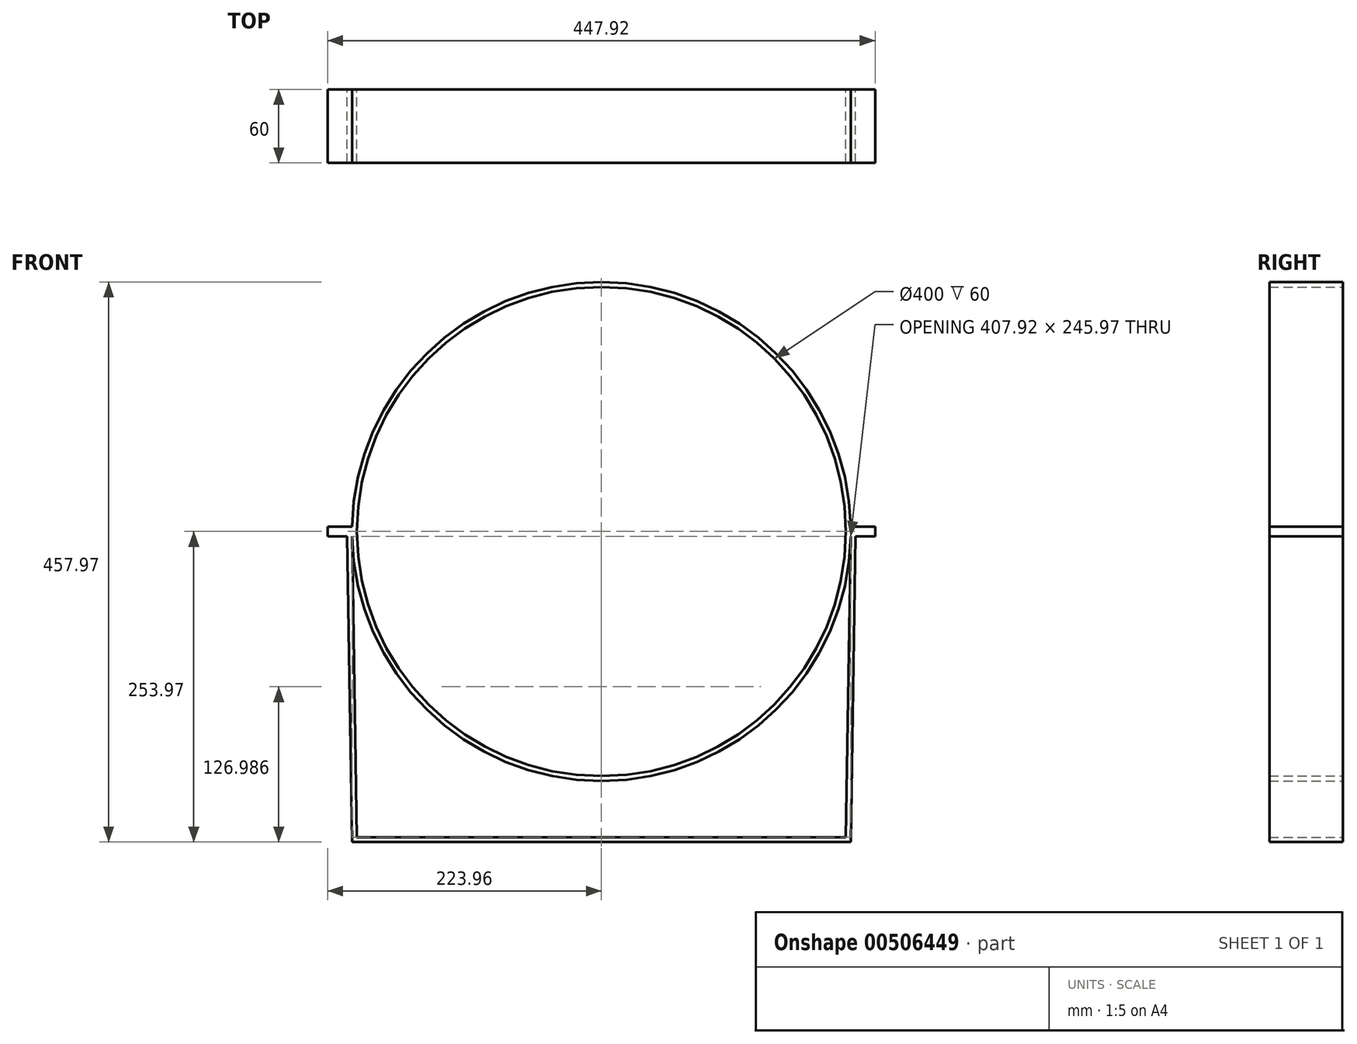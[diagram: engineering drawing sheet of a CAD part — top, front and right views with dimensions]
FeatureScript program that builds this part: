
annotation { "Feature Type Name" : "Feature", "Feature Type Description" : "" }
export const myFeature = defineFeature(function(context is Context, id is Id, definition is map)
    precondition{}
    {
        {
            var Q0;
            Q0=qCreatedBy(makeId("Front.planeOp"),FACE);
            var sketch = newSketch(context, id + "F0", { "sketchPlane" : qUnion([Q0])});
            skCircle(sketch, "E0", {"center": v(0, 0) * mm, "radius": 200 * mm});
            skCircle(sketch, "E1", {"center": v(0, 0) * mm, "radius": 204 * mm});
            skLineSegment(sketch, "E2", {"start": v(0, 0) * mm, "end": v(-690.21, 0) * mm, "construction": true});
            skLineSegment(sketch, "E3", {"start": v(-203.96, 4) * mm, "end": v(-223.96, 4) * mm});
            skLineSegment(sketch, "E4", {"start": v(-223.96, 4) * mm, "end": v(-223.96, 0) * mm});
            skLineSegment(sketch, "E5.MirrorCS", {"start": v(-203.96, -4) * mm, "end": v(-223.96, -4) * mm});
            skLineSegment(sketch, "E6.MirrorCS", {"start": v(-223.96, -4) * mm, "end": v(-223.96, 0) * mm});
            skLineSegment(sketch, "E7", {"start": v(0, 0) * mm, "end": v(0, 668.71) * mm, "construction": true});
            skLineSegment(sketch, "E8.MirrorCS", {"start": v(223.96, 4) * mm, "end": v(223.96, 0) * mm});
            skLineSegment(sketch, "E9.MirrorCS", {"start": v(223.96, -4) * mm, "end": v(223.96, 0) * mm});
            skLineSegment(sketch, "E10.MirrorCS", {"start": v(203.96, 4) * mm, "end": v(223.96, 4) * mm});
            skLineSegment(sketch, "E11.MirrorCS", {"start": v(203.96, -4) * mm, "end": v(223.96, -4) * mm});
            skLineSegment(sketch, "E12", {"start": v(-203.96, -4) * mm, "end": v(-207.96, -4) * mm});
            skLineSegment(sketch, "E13", {"start": v(-207.96, -4) * mm, "end": v(-203.96, -253.97) * mm});
            skLineSegment(sketch, "E14", {"start": v(-203.96, -4) * mm, "end": v(-200.02, -249.97) * mm});
            skLineSegment(sketch, "E15.MirrorCS", {"start": v(203.96, -4) * mm, "end": v(200.02, -249.97) * mm});
            skLineSegment(sketch, "E16.MirrorCS", {"start": v(207.96, -4) * mm, "end": v(203.96, -253.97) * mm});
            skLineSegment(sketch, "E17", {"start": v(-203.96, -253.97) * mm, "end": v(203.96, -253.97) * mm});
            skLineSegment(sketch, "E18", {"start": v(-200.02, -249.97) * mm, "end": v(200.02, -249.97) * mm});
            skSolve(sketch);
        }
        {
            var Q0;
            Q0=qSketchRegion(id+"F0",true);
            extrude(context, id + "F1", {"entities" : qUnion([Q0]), "offsetDistance" : 25 * mm, "depth" : 60 * mm});
        }
    });
